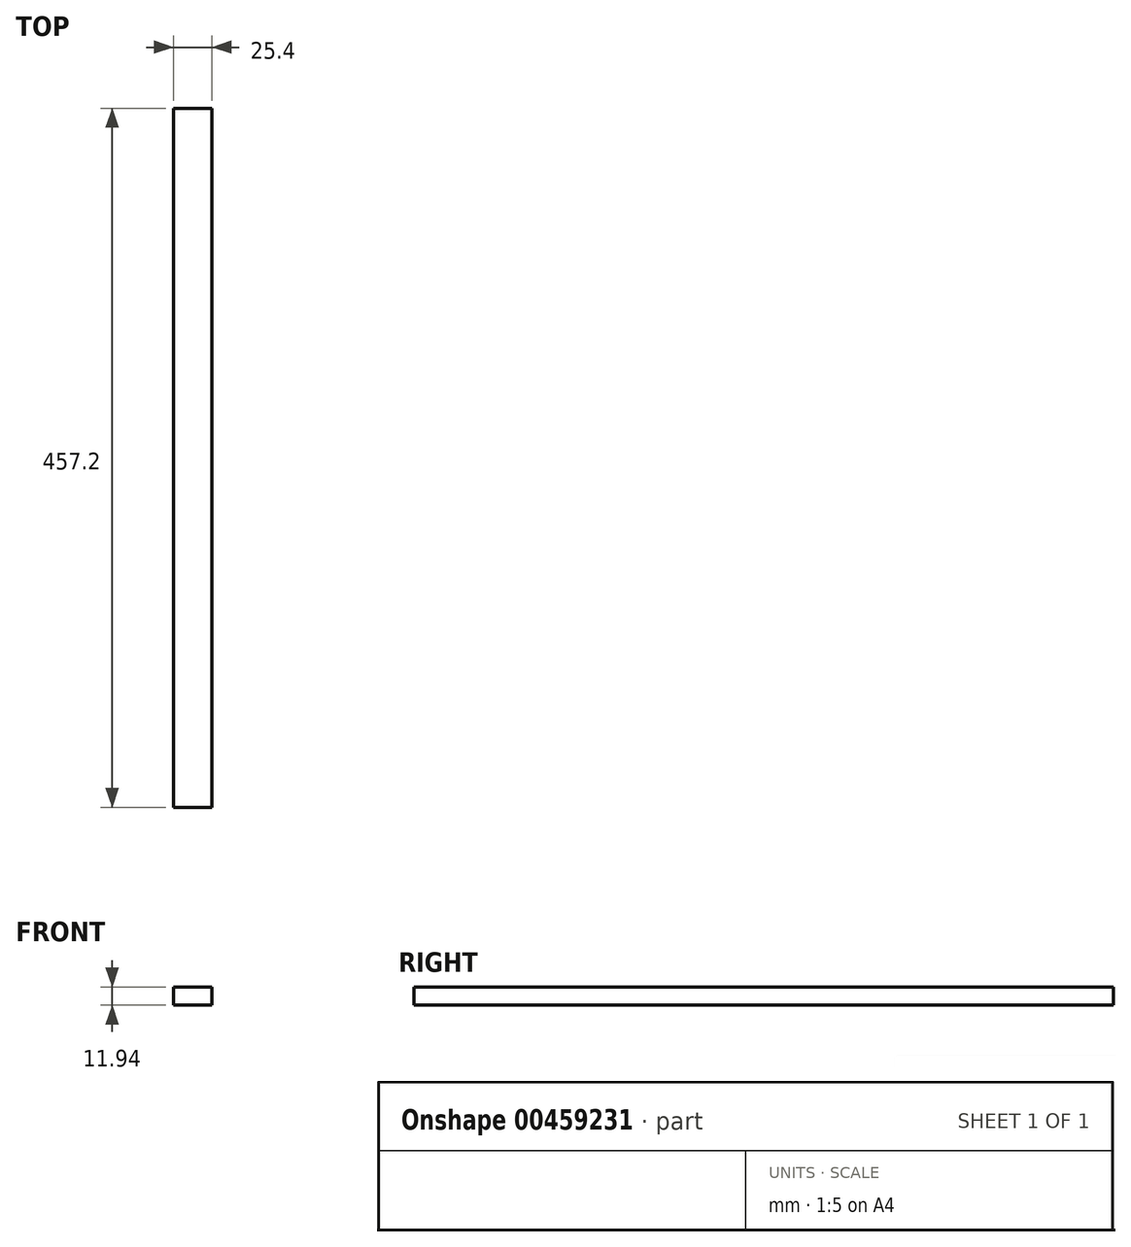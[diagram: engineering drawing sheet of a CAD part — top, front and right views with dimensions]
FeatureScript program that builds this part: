
annotation { "Feature Type Name" : "Feature", "Feature Type Description" : "" }
export const myFeature = defineFeature(function(context is Context, id is Id, definition is map)
    precondition{}
    {
        {
            var Q0;
            Q0=qCreatedBy(makeId("Front.planeOp"),FACE);
            var sketch = newSketch(context, id + "F0", { "sketchPlane" : qUnion([Q0])});
            skLineSegment(sketch, "E0.bottom", {"start": v(0, 0) * mm, "end": v(25.4, 0) * mm});
            skLineSegment(sketch, "E0.top", {"start": v(0, 11.94) * mm, "end": v(25.4, 11.94) * mm});
            skLineSegment(sketch, "E0.left", {"start": v(0, 0) * mm, "end": v(0, 11.94) * mm});
            skLineSegment(sketch, "E0.right", {"start": v(25.4, 0) * mm, "end": v(25.4, 11.94) * mm});
            skSolve(sketch);
        }
        {
            var Q0;
            Q0=makeQuery(id+"F0.imprint","IMPRINT",FACE,{"disambiguationData":[TD([[makeQuery(id+"F0.imprint","IMPRINT",EDGE,{"derivedFrom":sQuery(id+"F0.wireOp",EDGE,"E0.bottom")}),1.0]])]});
            extrude(context, id + "F1", {"entities" : qUnion([Q0]), "depth" : 457.2 * mm});
        }
    });
